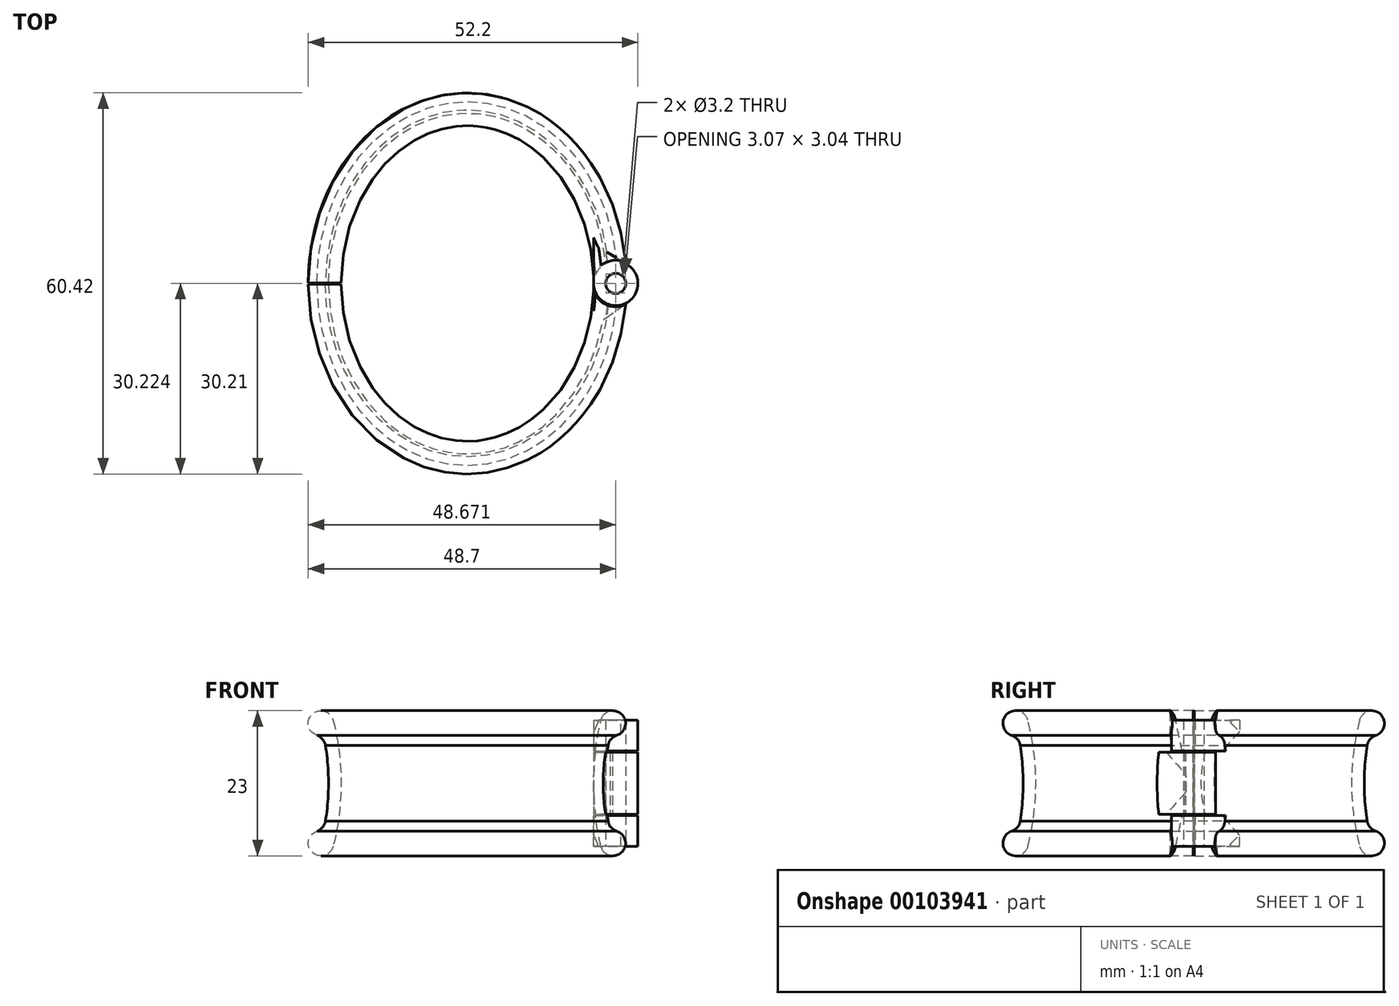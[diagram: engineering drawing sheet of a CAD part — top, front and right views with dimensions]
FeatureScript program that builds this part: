
annotation { "Feature Type Name" : "Feature", "Feature Type Description" : "" }
export const myFeature = defineFeature(function(context is Context, id is Id, definition is map)
    precondition{}
    {
        {
            var Q0;
            Q0=qCreatedBy(makeId("Top.planeOp"),FACE);
            var sketch = newSketch(context, id + "F0", { "sketchPlane" : qUnion([Q0])});
            skEllipse(sketch, "E0", {"center": v(0, 0) * mm, "majorRadius": 25 * mm, "minorRadius": 20 * mm, "majorAxis": v(0, 1)});
            skSolve(sketch);
        }
        {
            assignVariable(context, id + "F1", {"name" : "Bracelet_Width", "anyValue" : 20});
        }
        {
            var Q0;
            Q0=qCreatedBy(makeId("Front.planeOp"),FACE);
            var sketch = newSketch(context, id + "F2", { "sketchPlane" : qUnion([Q0])});
            skLineSegment(sketch, "E1.0", {"start": v(20, 0) * mm, "end": v(-20, 0) * mm, "construction": true});
            skArc(sketch, "E2", {"start": v(21.27, 10) * mm, "mid": v(20, 0) * mm, "end": v(21.27, -10) * mm});
            skArc(sketch, "E3", {"start": v(22.76, 7.55) * mm, "mid": v(24.92, 10.54) * mm, "end": v(21.27, 10) * mm});
            skArc(sketch, "E4", {"start": v(22.76, 7.55) * mm, "mid": v(22, 0) * mm, "end": v(22.76, -7.55) * mm});
            skArc(sketch, "E5", {"start": v(21.27, -10) * mm, "mid": v(24.92, -10.54) * mm, "end": v(22.76, -7.55) * mm});
            skLineSegment(sketch, "E6", {"start": v(21.27, 10) * mm, "end": v(21.27, -10) * mm, "construction": true});
            skLineSegment(sketch, "E7", {"start": v(20, 0) * mm, "end": v(22, 0) * mm, "construction": true});
            skSolve(sketch);
        }
        {
            var Q0;
            Q0 = qSketchRegion(id + "F2", true);
            var Q1;
            Q1 = qConstructionFilter(qBodyType(qCreatedBy(id + "F0" ,EDGE), BodyType.WIRE), ConstructionObject.NO);
            sweep(context, id + "F3", {"profiles" : qUnion([Q0]), "path" : qUnion([Q1])});
        }
        {
            var Q0;
            Q0=makeQuery(id+"F3.opSweep","SWEPT_FACE",FACE,{"disambiguationData":[OSD([sQuery(id+"F0.wireOp",EDGE,"E0"),sQuery(id+"F2.wireOp",EDGE,"E4")])]});
            fillet(context, id + "F4", {"entities" : qUnion([Q0]), "radius" : 2 * mm, "tangentPropagation" : true, "allowEdgeOverflow" : false});
        }
        {
            var Q0;
            Q0=qCreatedBy(makeId("Top.planeOp"),FACE);
            var sketch = newSketch(context, id + "F5", { "sketchPlane" : qUnion([Q0])});
            skFitSpline(sketch, "E8", {"points": [v(-20, 0) * mm, v(-20, -1.55) * mm, v(-19.88, -3.18) * mm, v(-19.63, -4.8) * mm, v(-19.61, -4.88) * mm, v(-19.37, -6.4) * mm, v(-19, -7.97) * mm, v(-18.5, -9.49) * mm, v(-18.48, -9.57) * mm, v(-18, -11) * mm, v(-17.4, -12.44) * mm, v(-16.67, -13.82) * mm, v(-16.63, -13.89) * mm, v(-15.94, -15.19) * mm, v(-15.11, -16.45) * mm, v(-14.2, -17.62) * mm, v(-14.14, -17.68) * mm, v(-13.27, -18.77) * mm, v(-12.26, -19.82) * mm, v(-11.17, -20.74) * mm, v(-11.11, -20.79) * mm, v(-10.07, -21.65) * mm, v(-8.92, -22.43) * mm, v(-7.72, -23.06) * mm, v(-7.65, -23.1) * mm, v(-6.5, -23.7) * mm, v(-5.26, -24.17) * mm, v(-3.97, -24.5) * mm, v(-3.9, -24.52) * mm, v(-2.68, -24.82) * mm, v(-1.38, -25) * mm, v(-0.07, -25) * mm, v(0, -25) * mm, v(1.24, -25) * mm, v(2.54, -24.85) * mm, v(3.83, -24.54) * mm, v(3.9, -24.52) * mm, v(5.13, -24.21) * mm, v(6.38, -23.75) * mm, v(7.6, -23.13) * mm, v(7.65, -23.1) * mm, v(8.8, -22.5) * mm, v(9.95, -21.74) * mm, v(11.05, -20.83) * mm, v(11.11, -20.79) * mm, v(12.15, -19.92) * mm, v(13.16, -18.89) * mm, v(14.1, -17.74) * mm, v(14.14, -17.68) * mm, v(15.02, -16.58) * mm, v(15.85, -15.32) * mm, v(16.59, -13.96) * mm, v(16.63, -13.89) * mm, v(17.32, -12.6) * mm, v(17.94, -11.15) * mm, v(18.45, -9.65) * mm, v(18.48, -9.57) * mm, v(18.95, -8.14) * mm, v(19.34, -6.57) * mm, v(19.6, -4.96) * mm, v(19.61, -4.88) * mm, v(19.86, -3.35) * mm, v(20, -1.72) * mm, v(20, -0.09) * mm, v(20, 0) * mm, v(20, 1.55) * mm, v(19.88, 3.18) * mm, v(19.63, 4.8) * mm, v(19.61, 4.88) * mm, v(19.37, 6.4) * mm, v(19, 7.97) * mm, v(18.5, 9.49) * mm, v(18.48, 9.57) * mm, v(18, 11) * mm, v(17.4, 12.44) * mm, v(16.67, 13.82) * mm, v(16.63, 13.89) * mm, v(15.94, 15.19) * mm, v(15.11, 16.45) * mm, v(14.2, 17.62) * mm, v(14.14, 17.68) * mm, v(13.27, 18.77) * mm, v(12.26, 19.82) * mm, v(11.17, 20.74) * mm, v(11.11, 20.79) * mm, v(10.07, 21.65) * mm, v(8.92, 22.43) * mm, v(7.72, 23.06) * mm, v(7.65, 23.1) * mm, v(6.5, 23.7) * mm, v(5.26, 24.17) * mm, v(3.97, 24.5) * mm, v(3.9, 24.52) * mm, v(2.68, 24.82) * mm, v(1.38, 25) * mm, v(0.07, 25) * mm, v(0, 25) * mm, v(-1.24, 25) * mm, v(-2.54, 24.85) * mm, v(-3.83, 24.54) * mm, v(-3.9, 24.52) * mm, v(-5.13, 24.21) * mm, v(-6.38, 23.75) * mm, v(-7.6, 23.13) * mm, v(-7.65, 23.1) * mm, v(-8.8, 22.5) * mm, v(-9.95, 21.74) * mm, v(-11.05, 20.83) * mm, v(-11.11, 20.79) * mm, v(-12.15, 19.92) * mm, v(-13.16, 18.89) * mm, v(-14.1, 17.74) * mm, v(-14.14, 17.68) * mm, v(-15.02, 16.58) * mm, v(-15.85, 15.32) * mm, v(-16.59, 13.96) * mm, v(-16.63, 13.89) * mm, v(-17.32, 12.6) * mm, v(-17.94, 11.15) * mm, v(-18.45, 9.65) * mm, v(-18.48, 9.57) * mm, v(-18.95, 8.14) * mm, v(-19.34, 6.57) * mm, v(-19.6, 4.96) * mm, v(-19.61, 4.88) * mm, v(-19.87, 3.26) * mm, v(-20, 1.64) * mm, v(-20, 0) * mm, v(-20, 0) * mm], "construction": true});
            skFitSpline(sketch, "E9", {"points": [v(-25.2, -0.72) * mm, v(-25.24, 1.1) * mm, v(-25.13, 3) * mm, v(-24.88, 4.9) * mm, v(-24.86, 4.99) * mm, v(-24.61, 6.79) * mm, v(-24.21, 8.64) * mm, v(-23.66, 10.44) * mm, v(-23.63, 10.53) * mm, v(-23.1, 12.25) * mm, v(-22.42, 13.98) * mm, v(-21.58, 15.64) * mm, v(-21.54, 15.73) * mm, v(-20.74, 17.31) * mm, v(-19.77, 18.87) * mm, v(-18.68, 20.32) * mm, v(-18.63, 20.4) * mm, v(-17.57, 21.78) * mm, v(-16.36, 23.1) * mm, v(-15.02, 24.29) * mm, v(-14.95, 24.35) * mm, v(-14.32, 24.9) * mm, v(-13.62, 25.46) * mm, v(-12.9, 25.97) * mm, v(-12.87, 26) * mm, v(-12.18, 26.49) * mm, v(-11.43, 26.96) * mm, v(-10.67, 27.39) * mm, v(-10.63, 27.4) * mm, v(-9.16, 28.22) * mm, v(-7.55, 28.9) * mm, v(-5.87, 29.38) * mm, v(-5.79, 29.4) * mm, v(-5, 29.62) * mm, v(-4.14, 29.81) * mm, v(-3.29, 29.95) * mm, v(-3.24, 29.96) * mm, v(-2.42, 30.08) * mm, v(-1.56, 30.17) * mm, v(-0.7, 30.2) * mm, v(-0.65, 30.2) * mm, v(0.17, 30.22) * mm, v(1.03, 30.2) * mm, v(1.9, 30.12) * mm, v(1.95, 30.12) * mm, v(2.76, 30.04) * mm, v(3.62, 29.9) * mm, v(4.48, 29.73) * mm, v(4.52, 29.72) * mm, v(5.32, 29.54) * mm, v(6.16, 29.31) * mm, v(7, 29.03) * mm, v(7.03, 29.01) * mm, v(7.82, 28.74) * mm, v(8.63, 28.41) * mm, v(9.42, 28.03) * mm, v(9.46, 28.01) * mm, v(10.2, 27.66) * mm, v(10.97, 27.23) * mm, v(11.72, 26.76) * mm, v(11.76, 26.74) * mm, v(12.47, 26.3) * mm, v(13.2, 25.79) * mm, v(13.9, 25.23) * mm, v(13.93, 25.2) * mm, v(14.59, 24.68) * mm, v(15.26, 24.1) * mm, v(15.9, 23.47) * mm, v(15.94, 23.44) * mm, v(16.55, 22.84) * mm, v(17.16, 22.19) * mm, v(17.75, 21.5) * mm, v(17.78, 21.46) * mm, v(18.87, 20.15) * mm, v(19.92, 18.66) * mm, v(20.84, 17.03) * mm, v(20.89, 16.95) * mm, v(21.74, 15.43) * mm, v(22.52, 13.74) * mm, v(23.16, 11.96) * mm, v(23.2, 11.87) * mm, v(23.78, 10.2) * mm, v(24.27, 8.38) * mm, v(24.62, 6.5) * mm, v(24.64, 6.4) * mm, v(24.96, 4.62) * mm, v(25.15, 2.73) * mm, v(25.2, 0.82) * mm, v(25.2, 0.72) * mm, v(25.24, -1.1) * mm, v(25.13, -3) * mm, v(24.88, -4.9) * mm, v(24.86, -4.99) * mm, v(24.61, -6.79) * mm, v(24.21, -8.64) * mm, v(23.66, -10.44) * mm, v(23.63, -10.53) * mm, v(23.1, -12.25) * mm, v(22.42, -13.98) * mm, v(21.58, -15.64) * mm, v(21.54, -15.73) * mm, v(20.74, -17.31) * mm, v(19.77, -18.87) * mm, v(18.68, -20.32) * mm, v(18.63, -20.4) * mm, v(17.57, -21.78) * mm, v(16.36, -23.1) * mm, v(15.02, -24.29) * mm, v(14.95, -24.35) * mm, v(14.32, -24.9) * mm, v(13.62, -25.46) * mm, v(12.9, -25.97) * mm, v(12.87, -26) * mm, v(12.18, -26.49) * mm, v(11.43, -26.96) * mm, v(10.67, -27.39) * mm, v(10.63, -27.4) * mm, v(9.16, -28.22) * mm, v(7.55, -28.9) * mm, v(5.87, -29.38) * mm, v(5.79, -29.4) * mm, v(5, -29.62) * mm, v(4.14, -29.81) * mm, v(3.29, -29.95) * mm, v(3.24, -29.96) * mm, v(2.42, -30.08) * mm, v(1.56, -30.17) * mm, v(0.7, -30.2) * mm, v(0.65, -30.2) * mm, v(-0.17, -30.22) * mm, v(-1.03, -30.2) * mm, v(-1.9, -30.12) * mm, v(-1.95, -30.12) * mm, v(-2.76, -30.04) * mm, v(-3.62, -29.9) * mm, v(-4.48, -29.73) * mm, v(-4.52, -29.72) * mm, v(-5.32, -29.54) * mm, v(-6.16, -29.31) * mm, v(-7, -29.03) * mm, v(-7.03, -29.01) * mm, v(-7.82, -28.74) * mm, v(-8.63, -28.41) * mm, v(-9.42, -28.03) * mm, v(-9.46, -28.01) * mm, v(-10.2, -27.66) * mm, v(-10.97, -27.23) * mm, v(-11.72, -26.76) * mm, v(-11.76, -26.74) * mm, v(-12.47, -26.3) * mm, v(-13.2, -25.79) * mm, v(-13.9, -25.23) * mm, v(-13.93, -25.2) * mm, v(-14.59, -24.68) * mm, v(-15.26, -24.1) * mm, v(-15.9, -23.47) * mm, v(-15.94, -23.44) * mm, v(-16.55, -22.84) * mm, v(-17.16, -22.19) * mm, v(-17.75, -21.5) * mm, v(-17.78, -21.46) * mm, v(-18.87, -20.15) * mm, v(-19.92, -18.66) * mm, v(-20.84, -17.03) * mm, v(-20.89, -16.95) * mm, v(-21.74, -15.43) * mm, v(-22.52, -13.74) * mm, v(-23.16, -11.96) * mm, v(-23.2, -11.87) * mm, v(-23.78, -10.2) * mm, v(-24.27, -8.38) * mm, v(-24.62, -6.5) * mm, v(-24.64, -6.4) * mm, v(-24.97, -4.52) * mm, v(-25.16, -2.63) * mm, v(-25.2, -0.72) * mm, v(-25.2, -0.72) * mm], "construction": true});
            skLineSegment(sketch, "E10", {"start": v(20, 0) * mm, "end": v(25.2, 0) * mm, "construction": true});
            skCircle(sketch, "E11", {"center": v(23.5, 0) * mm, "radius": 3.5 * mm});
            skCircle(sketch, "E12", {"center": v(23.5, 0) * mm, "radius": 1.6 * mm});
            skSolve(sketch);
        }
        {
            var Q0;
            Q0=qCreatedBy(makeId("Top.planeOp"),FACE);
            var sketch = newSketch(context, id + "F6", { "sketchPlane" : qUnion([Q0])});
            skCircle(sketch, "E13.0", {"center": v(23.5, 0) * mm, "radius": 3.5 * mm, "construction": true});
            skCircle(sketch, "E14", {"center": v(23.5, 0) * mm, "radius": 3.7 * mm});
            skSolve(sketch);
        }
        {
            var Q0;
            Q0 = qSketchRegion(id + "F6", true);
            extrude(context, id + "F7", {"entities" : qUnion([Q0]), "operationType" : NewBodyOperationType.REMOVE, "endBound" : BoundingType.SYMMETRIC, "oppositeDirection" : true, "depth" : 25 * mm});
        }
        {
            var Q0;
            Q0 = qSketchRegion(id + "F5", true);
            var Q1;
            Q1=makeQuery(id+"F3.opSweep","SWEPT_FACE",FACE,{"disambiguationData":[OSD([sQuery(id+"F0.wireOp",EDGE,"E0"),sQuery(id+"F2.wireOp",EDGE,"E3")])]});
            var Q2;
            Q2=makeQuery(id+"F3.opSweep","SWEPT_FACE",FACE,{"disambiguationData":[OSD([sQuery(id+"F0.wireOp",EDGE,"E0"),sQuery(id+"F2.wireOp",EDGE,"E5")])]});
            extrude(context, id + "F8", {"entities" : qUnion([Q0]), "endBound" : BoundingType.SYMMETRIC, "endBoundEntityFace" : qUnion([Q1]), "depth" : (getVariable(context, 'Bracelet_Width')) * mm});
        }
        {
            var Q0;
            Q0 = qSketchRegion(id + "F6", true);
            extrude(context, id + "F9", {"entities" : qUnion([Q0]), "operationType" : NewBodyOperationType.REMOVE, "endBound" : BoundingType.SYMMETRIC, "oppositeDirection" : true, "depth" : (getVariable(context, 'Bracelet_Width') / 2 + 0.2) * mm, "hasSecondDirection" : true, "secondDirectionOppositeDirection" : false, "secondDirectionDepth" : 5.52 * mm});
        }
        {
            var Q0;
            Q0 = qSketchRegion(id + "F5", true);
            extrude(context, id + "F10", {"entities" : qUnion([Q0]), "operationType" : NewBodyOperationType.ADD, "endBound" : BoundingType.SYMMETRIC, "depth" : (getVariable(context, 'Bracelet_Width') / 2 - 0.1) * mm});
        }
        {
            var Q0;
            Q0=qCreatedBy(makeId("Front.planeOp"),FACE);
            var sketch = newSketch(context, id + "F11", { "sketchPlane" : qUnion([Q0])});
            skLineSegment(sketch, "E15.bottom", {"start": v(-12.77, 13.1) * mm, "end": v(-30.84, 13.1) * mm});
            skLineSegment(sketch, "E15.top", {"start": v(-12.77, -13.55) * mm, "end": v(-30.84, -13.55) * mm});
            skLineSegment(sketch, "E15.left", {"start": v(-12.77, 13.1) * mm, "end": v(-12.77, -13.55) * mm});
            skLineSegment(sketch, "E15.right", {"start": v(-30.84, 13.1) * mm, "end": v(-30.84, -13.55) * mm});
            skSolve(sketch);
        }
        {
            var Q0;
            Q0 = qSketchRegion(id + "F11", true);
            extrude(context, id + "F12", {"entities" : qUnion([Q0]), "operationType" : NewBodyOperationType.REMOVE, "endBound" : BoundingType.SYMMETRIC, "oppositeDirection" : true, "depth" : 0.2 * mm});
        }
        {
            var Q0;
            Q0=qCreatedBy(makeId("Top.planeOp"),FACE);
            var sketch = newSketch(context, id + "F13", { "sketchPlane" : qUnion([Q0])});
            skCircle(sketch, "E16.0", {"center": v(23.5, 0) * mm, "radius": 3.5 * mm, "construction": true});
            skFitSpline(sketch, "E17.0.0", {"points": [v(21.27, 0) * mm, v(1000, 21.27) * mm, v(-3.4, 1000) * mm, v(20.73, -6.8) * mm, v(1000, 18.64) * mm, v(-13.12, 1000) * mm, v(17.09, -16.03) * mm, v(1000, 13.18) * mm, v(-20.91, 1000) * mm, v(10.83, -22.88) * mm, v(1000, 5.65) * mm, v(-25.57, 1000) * mm, v(2.83, -26.27) * mm, v(1000, -2.83) * mm, v(-26.27, 1000) * mm, v(-5.65, -25.57) * mm, v(1000, -10.83) * mm, v(-22.88, 1000) * mm, v(-13.18, -20.91) * mm, v(1000, -17.09) * mm, v(-16.03, 1000) * mm, v(-18.64, -13.12) * mm, v(1000, -20.73) * mm, v(-6.8, 1000) * mm, v(-21.27, -3.4) * mm, v(1000, -21.27) * mm, v(3.4, 1000) * mm, v(-20.73, 6.8) * mm, v(1000, -18.64) * mm, v(13.12, 1000) * mm, v(-17.09, 16.03) * mm, v(1000, -13.18) * mm, v(20.91, 1000) * mm, v(-10.83, 22.88) * mm], "construction": true});
            skFitSpline(sketch, "E17.0.2", {"points": [v(21.27, 0) * mm, v(1000, 21.27) * mm, v(3.4, 1000) * mm, v(20.73, 6.8) * mm, v(1000, 18.64) * mm, v(13.12, 1000) * mm, v(17.09, 16.03) * mm, v(1000, 13.18) * mm, v(20.91, 1000) * mm, v(10.83, 22.88) * mm, v(1000, 5.65) * mm, v(25.57, 1000) * mm, v(2.83, 26.27) * mm, v(1000, -2.83) * mm, v(26.27, 1000) * mm, v(-5.65, 25.57) * mm, v(1000, -10.83) * mm, v(22.88, 1000) * mm, v(-13.18, 20.91) * mm, v(1000, -17.09) * mm, v(16.03, 1000) * mm, v(-18.64, 13.12) * mm, v(1000, -20.73) * mm, v(6.8, 1000) * mm, v(-21.27, 3.4) * mm, v(1000, -21.27) * mm, v(-3.4, 1000) * mm, v(-20.73, -6.8) * mm, v(1000, -18.64) * mm, v(-13.12, 1000) * mm, v(-17.09, -16.03) * mm, v(1000, -13.18) * mm, v(-20.91, 1000) * mm, v(-10.83, -22.88) * mm], "construction": true});
            skFitSpline(sketch, "E18.0.0", {"points": [v(21.27, 0) * mm, v(1000, 21.27) * mm, v(-3.4, 1000) * mm, v(20.73, -6.8) * mm, v(1000, 18.64) * mm, v(-13.12, 1000) * mm, v(17.09, -16.03) * mm, v(1000, 13.18) * mm, v(-20.91, 1000) * mm, v(10.83, -22.88) * mm, v(1000, 5.65) * mm, v(-25.57, 1000) * mm, v(2.83, -26.27) * mm, v(1000, -2.83) * mm, v(-26.27, 1000) * mm, v(-5.65, -25.57) * mm, v(1000, -10.83) * mm, v(-22.88, 1000) * mm, v(-13.18, -20.91) * mm, v(1000, -17.09) * mm, v(-16.03, 1000) * mm, v(-18.64, -13.12) * mm, v(1000, -20.73) * mm, v(-6.8, 1000) * mm, v(-21.27, -3.4) * mm, v(1000, -21.27) * mm, v(3.4, 1000) * mm, v(-20.73, 6.8) * mm, v(1000, -18.64) * mm, v(13.12, 1000) * mm, v(-17.09, 16.03) * mm, v(1000, -13.18) * mm, v(20.91, 1000) * mm, v(-10.83, 22.88) * mm], "construction": true});
            skFitSpline(sketch, "E18.0.2", {"points": [v(21.27, 0) * mm, v(1000, 21.27) * mm, v(3.4, 1000) * mm, v(20.73, 6.8) * mm, v(1000, 18.64) * mm, v(13.12, 1000) * mm, v(17.09, 16.03) * mm, v(1000, 13.18) * mm, v(20.91, 1000) * mm, v(10.83, 22.88) * mm, v(1000, 5.65) * mm, v(25.57, 1000) * mm, v(2.83, 26.27) * mm, v(1000, -2.83) * mm, v(26.27, 1000) * mm, v(-5.65, 25.57) * mm, v(1000, -10.83) * mm, v(22.88, 1000) * mm, v(-13.18, 20.91) * mm, v(1000, -17.09) * mm, v(16.03, 1000) * mm, v(-18.64, 13.12) * mm, v(1000, -20.73) * mm, v(6.8, 1000) * mm, v(-21.27, 3.4) * mm, v(1000, -21.27) * mm, v(-3.4, 1000) * mm, v(-20.73, -6.8) * mm, v(1000, -18.64) * mm, v(-13.12, 1000) * mm, v(-17.09, -16.03) * mm, v(1000, -13.18) * mm, v(-20.91, 1000) * mm, v(-10.83, -22.88) * mm], "construction": true});
            skLineSegment(sketch, "E19", {"start": v(20, 0) * mm, "end": v(20, -9.29) * mm});
            skLineSegment(sketch, "E20", {"start": v(20, -9.29) * mm, "end": v(21, -6.15) * mm});
            skLineSegment(sketch, "E21", {"start": v(21, -6.15) * mm, "end": v(25.56, -2.83) * mm});
            skLineSegment(sketch, "E22", {"start": v(25.56, -2.83) * mm, "end": v(20, 0) * mm});
            skSolve(sketch);
        }
        {
            var Q0;
            Q0 = qSketchRegion(id + "F13", true);
            var Q1;
            Q1=makeQuery(id+"F10.opExtrude","CAP_FACE",FACE,{"disambiguationData":[OSD([sQuery(id+"F5.wireOp",EDGE,"E11"),sQuery(id+"F5.wireOp",EDGE,"E12")])],"isStart":false});
            var Q2;
            Q2=makeQuery(id+"F10.opExtrude","SWEPT_BODY",BODY,{"disambiguationData":[OSD([sQuery(id+"F5.wireOp",EDGE,"E11"),sQuery(id+"F5.wireOp",EDGE,"E12")])]});
            var Q3;
            Q3=makeQuery(id+"F10.opExtrude","CAP_FACE",FACE,{"disambiguationData":[OSD([sQuery(id+"F5.wireOp",EDGE,"E11"),sQuery(id+"F5.wireOp",EDGE,"E12")])],"isStart":true});
            var Q4;
            Q4=makeQuery(id+"F10.opExtrude","SWEPT_BODY",BODY,{"disambiguationData":[OSD([sQuery(id+"F5.wireOp",EDGE,"E11"),sQuery(id+"F5.wireOp",EDGE,"E12")])]});
            extrude(context, id + "F14", {"entities" : qUnion([Q0]), "operationType" : NewBodyOperationType.ADD, "endBound" : BoundingType.UP_TO_SURFACE, "endBoundEntityFace" : qUnion([Q1]), "endBoundEntityBody" : qUnion([Q2]), "depth" : 4.5 * mm, "hasSecondDirection" : true, "secondDirectionBound" : SecondDirectionBoundingType.UP_TO_SURFACE, "secondDirectionOppositeDirection" : true, "secondDirectionBoundEntityFace" : qUnion([Q3]), "secondDirectionBoundEntityBody" : qUnion([Q4]), "secondDirectionDepth" : 4.5 * mm});
        }
        {
            var Q0;
            Q0=makeQuery(id+"F9.boolean.opBoolean","COPY",FACE,{"derivedFrom":makeQuery(id+"F9.opExtrude","CAP_FACE",FACE,{"disambiguationData":[OSD([sQuery(id+"F6.wireOp",EDGE,"E14")])],"isStart":true})});
            var sketch = newSketch(context, id + "F15", { "sketchPlane" : qUnion([Q0])});
            skLineSegment(sketch, "E23", {"start": v(20, 0.24) * mm, "end": v(20, -7.27) * mm});
            skLineSegment(sketch, "E24", {"start": v(20, -7.27) * mm, "end": v(20.63, -5.85) * mm});
            skLineSegment(sketch, "E25", {"start": v(20.63, -5.85) * mm, "end": v(25.32, -2.99) * mm});
            skLineSegment(sketch, "E26", {"start": v(25.32, -2.99) * mm, "end": v(20, 0.24) * mm});
            skSolve(sketch);
        }
        {
            var Q0;
            Q0 = qSketchRegion(id + "F15", true);
            var Q1;
            Q1=makeQuery(id+"F8.opExtrude","CAP_FACE",FACE,{"disambiguationData":[OSD([sQuery(id+"F5.wireOp",EDGE,"E11"),sQuery(id+"F5.wireOp",EDGE,"E12")])],"isStart":false});
            extrude(context, id + "F16", {"entities" : qUnion([Q0]), "operationType" : NewBodyOperationType.ADD, "endBound" : BoundingType.UP_TO_SURFACE, "oppositeDirection" : true, "endBoundEntityFace" : qUnion([Q1]), "depth" : 25 * mm});
        }
        {
            var Q0;
            Q0=makeQuery(id+"F9.boolean.opBoolean","COPY",FACE,{"derivedFrom":makeQuery(id+"F9.opExtrude","CAP_FACE",FACE,{"disambiguationData":[OSD([sQuery(id+"F6.wireOp",EDGE,"E14")])],"isStart":false})});
            var sketch = newSketch(context, id + "F17", { "sketchPlane" : qUnion([Q0])});
            skLineSegment(sketch, "E27.0", {"start": v(20, -0.24) * mm, "end": v(20, 7.27) * mm});
            skLineSegment(sketch, "E28.0", {"start": v(20, 7.27) * mm, "end": v(20.63, 5.85) * mm});
            skLineSegment(sketch, "E29.0", {"start": v(20.63, 5.85) * mm, "end": v(25.32, 2.99) * mm});
            skLineSegment(sketch, "E30.0", {"start": v(25.32, 2.99) * mm, "end": v(20, -0.24) * mm});
            skSolve(sketch);
        }
        {
            var Q0;
            Q0 = qSketchRegion(id + "F17", true);
            var Q1;
            Q1=makeQuery(id+"F8.opExtrude","CAP_FACE",FACE,{"disambiguationData":[OSD([sQuery(id+"F5.wireOp",EDGE,"E11"),sQuery(id+"F5.wireOp",EDGE,"E12")])],"isStart":true});
            extrude(context, id + "F18", {"entities" : qUnion([Q0]), "operationType" : NewBodyOperationType.ADD, "endBound" : BoundingType.UP_TO_SURFACE, "oppositeDirection" : true, "endBoundEntityFace" : qUnion([Q1]), "depth" : 25 * mm});
        }
    });
